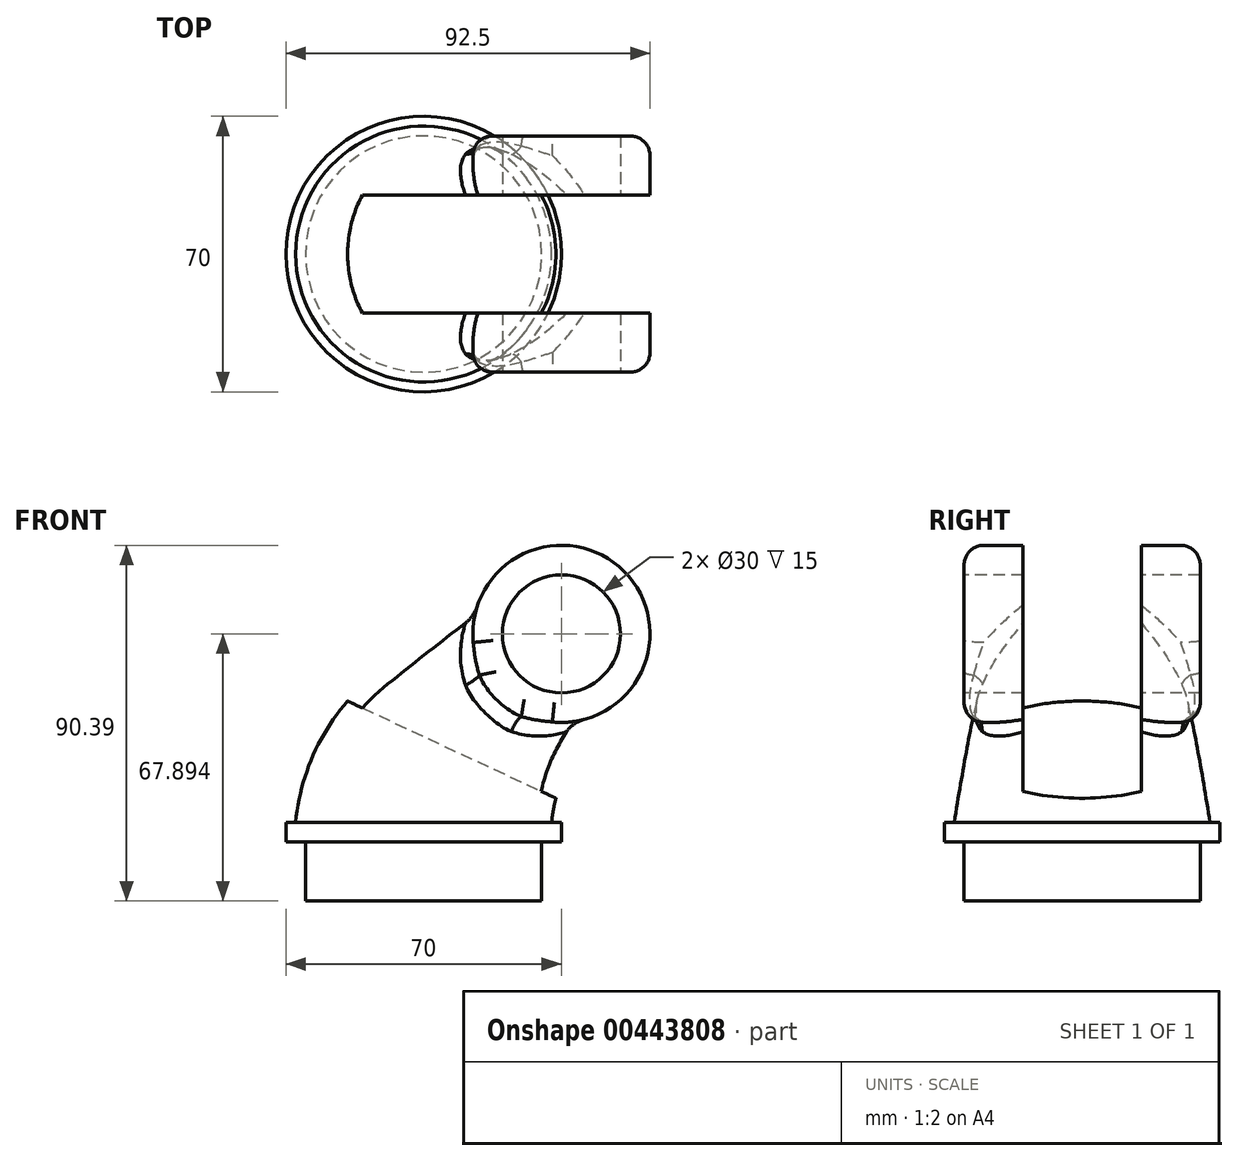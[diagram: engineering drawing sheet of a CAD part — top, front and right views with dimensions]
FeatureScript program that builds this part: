
annotation { "Feature Type Name" : "Feature", "Feature Type Description" : "" }
export const myFeature = defineFeature(function(context is Context, id is Id, definition is map)
    precondition{}
    {
        {
            var Q0;
            Q0=qCreatedBy(makeId("Top.planeOp"),FACE);
            var sketch = newSketch(context, id + "F0", { "sketchPlane" : qUnion([Q0])});
            skCircle(sketch, "E0", {"center": v(0, 0) * mm, "radius": 35 * mm});
            skSolve(sketch);
        }
        {
            var Q0;
            Q0 = qSketchRegion(id + "F0", true);
            extrude(context, id + "F1", {"entities" : qUnion([Q0]), "depth" : 5 * mm});
        }
        {
            var Q0;
            Q0=qCreatedBy(makeId("Front.planeOp"),FACE);
            var sketch = newSketch(context, id + "F2", { "sketchPlane" : qUnion([Q0])});
            skArc(sketch, "E1", {"start": v(17.6, 38.3) * mm, "mid": v(5.55, 23.37) * mm, "end": v(0, 5) * mm});
            skLineSegment(sketch, "E2", {"start": v(17.6, 38.3) * mm, "end": v(35, 52.9) * mm});
            skSolve(sketch);
        }
        {
            var Q0;
            Q0=sQuery(id+"F2.wireOp",EDGE,"E2");
            var Q1;
            Q1=sQuery(id+"F2.wireOp",VERTEX,"E2.end");
            cPlane(context, id + "F3", {"entities" : qUnion([Q0, Q1]), "cplaneType" : CPlaneType.LINE_POINT, "offset" : 25 * mm, "width" : 150 * mm, "height" : 150 * mm});
        }
        {
            var Q0;
            Q0=qCreatedBy(id+"F3.planeOp",FACE);
            var sketch = newSketch(context, id + "F4", { "sketchPlane" : qUnion([Q0])});
            skCircle(sketch, "E3", {"center": v(0, 18.02) * mm, "radius": 22.5 * mm});
            skSolve(sketch);
        }
        {
            var Q0;
            Q0=makeQuery(id+"F1.opExtrude","CAP_FACE",FACE,{"disambiguationData":[OSD([sQuery(id+"F0.wireOp",EDGE,"E0")])],"isStart":false});
            var sketch = newSketch(context, id + "F5", { "sketchPlane" : qUnion([Q0])});
            skCircle(sketch, "E4", {"center": v(0, 0) * mm, "radius": 32.5 * mm});
            skSolve(sketch);
        }
        {
            var Q0;
            Q0=qCreatedBy(makeId("Front.planeOp"),FACE);
            var sketch = newSketch(context, id + "F6", { "sketchPlane" : qUnion([Q0])});
            skArc(sketch, "E5", {"start": v(-13.25, 41.78) * mm, "mid": v(-26.5, 25.3) * mm, "end": v(-32.5, 5) * mm});
            skLineSegment(sketch, "E6", {"start": v(-13.25, 41.78) * mm, "end": v(20.54, 70.13) * mm});
            skSolve(sketch);
        }
        {
            var Q0;
            Q0=qCreatedBy(makeId("Front.planeOp"),FACE);
            var sketch = newSketch(context, id + "F7", { "sketchPlane" : qUnion([Q0])});
            skArc(sketch, "E7", {"start": v(48.46, 34.82) * mm, "mid": v(37.6, 21.45) * mm, "end": v(32.5, 5) * mm});
            skLineSegment(sketch, "E8", {"start": v(48.46, 34.82) * mm, "end": v(49.46, 35.66) * mm});
            skSolve(sketch);
        }
        {
            var Q1;
            Q1=makeQuery(id+"F5.imprint","IMPRINT",FACE,{"disambiguationData":[TD([[makeQuery(id+"F5.imprint","IMPRINT",EDGE,{"derivedFrom":sQuery(id+"F5.wireOp",EDGE,"E4")}),1.0]])]});
            var Q2;
            Q2=makeQuery(id+"F4.imprint","IMPRINT",FACE,{"disambiguationData":[TD([[makeQuery(id+"F4.imprint","IMPRINT",EDGE,{"derivedFrom":sQuery(id+"F4.wireOp",EDGE,"E3")}),1.0]])]});
            var Q3;
            Q3 = qConstructionFilter(qBodyType(qCreatedBy(id + "F6" ,EDGE), BodyType.WIRE), ConstructionObject.NO);
            var Q4;
            Q4 = qConstructionFilter(qBodyType(qCreatedBy(id + "F7" ,EDGE), BodyType.WIRE), ConstructionObject.NO);
            loft(context, id + "F8", {"operationType" : NewBodyOperationType.ADD, "addGuides" : true, "sheetProfilesArray" : [{ "sheetProfileEntities" : qUnion([Q1]) }, { "sheetProfileEntities" : qUnion([Q2]) }], "guidesArray" : [{ "guideEntities" : qUnion([Q3]), "guideDerivativeType" : LoftGuideDerivativeType.DEFAULT, "guideDerivativeMagnitude" : 1 }, { "guideEntities" : qUnion([Q4]), "guideDerivativeType" : LoftGuideDerivativeType.DEFAULT, "guideDerivativeMagnitude" : 1 }]});
        }
        {
            var Q0;
            Q0=qCreatedBy(makeId("Front.planeOp"),FACE);
            var sketch = newSketch(context, id + "F9", { "sketchPlane" : qUnion([Q0])});
            skCircle(sketch, "E9", {"center": v(35, 52.9) * mm, "radius": 22.5 * mm});
            skSolve(sketch);
        }
        {
            var Q0;
            Q0 = qSketchRegion(id + "F9", true);
            extrude(context, id + "F10", {"entities" : qUnion([Q0]), "operationType" : NewBodyOperationType.ADD, "endBound" : BoundingType.SYMMETRIC, "depth" : 60 * mm});
        }
        {
            var Q0;
            Q0=makeQuery(id+"F10.boolean.opBoolean","INTERSECT",EDGE,{"disambiguationData":[OD(1.0)],"derivedFrom":[makeQuery(id+"F8.opLoft","SWEPT_FACE",FACE,{"disambiguationData":[OSD([sQuery(id+"F4.wireOp",EDGE,"E3"),sQuery(id+"F5.wireOp",EDGE,"E4"),sQuery(id+"F6.wireOp",VERTEX,"E6.start"),sQuery(id+"F6.wireOp",EDGE,"E5"),sQuery(id+"F6.wireOp",EDGE,"E6"),sQuery(id+"F7.wireOp",VERTEX,"E8.start"),sQuery(id+"F7.wireOp",EDGE,"E7"),sQuery(id+"F7.wireOp",EDGE,"E8")])]}),makeQuery(id+"F10.opExtrude","SWEPT_FACE",FACE,{"disambiguationData":[OSD([sQuery(id+"F9.wireOp",EDGE,"E9")])]})]});
            var Q1;
            Q1=makeQuery(id+"F10.boolean.opBoolean","INTERSECT",EDGE,{"disambiguationData":[OD(0.0)],"derivedFrom":[makeQuery(id+"F8.opLoft","SWEPT_FACE",FACE,{"disambiguationData":[OSD([sQuery(id+"F4.wireOp",EDGE,"E3"),sQuery(id+"F5.wireOp",EDGE,"E4"),sQuery(id+"F6.wireOp",VERTEX,"E6.start"),sQuery(id+"F6.wireOp",EDGE,"E5"),sQuery(id+"F6.wireOp",EDGE,"E6"),sQuery(id+"F7.wireOp",VERTEX,"E8.start"),sQuery(id+"F7.wireOp",EDGE,"E7"),sQuery(id+"F7.wireOp",EDGE,"E8")])]}),makeQuery(id+"F10.opExtrude","SWEPT_FACE",FACE,{"disambiguationData":[OSD([sQuery(id+"F9.wireOp",EDGE,"E9")])]})]});
            fillet(context, id + "F11", {"entities" : qUnion([Q0, Q1]), "radius" : 5 * mm, "tangentPropagation" : true, "allowEdgeOverflow" : false});
        }
        {
            var Q0;
            Q0=makeQuery(id+"F10.opExtrude","CAP_FACE",FACE,{"disambiguationData":[OSD([sQuery(id+"F9.wireOp",EDGE,"E9")])],"isStart":true});
            var Q1;
            Q1=makeQuery(id+"F10.opExtrude","CAP_FACE",FACE,{"disambiguationData":[OSD([sQuery(id+"F9.wireOp",EDGE,"E9")])],"isStart":false});
            fillet(context, id + "F12", {"entities" : qUnion([Q0, Q1]), "radius" : 5 * mm, "tangentPropagation" : true, "allowEdgeOverflow" : false});
        }
        {
            var Q0;
            Q0=makeQuery(id+"F10.opExtrude","CAP_FACE",FACE,{"disambiguationData":[OSD([sQuery(id+"F9.wireOp",EDGE,"E9")])],"isStart":false});
            var sketch = newSketch(context, id + "F13", { "sketchPlane" : qUnion([Q0])});
            skCircle(sketch, "E10", {"center": v(35, 52.9) * mm, "radius": 15 * mm});
            skSolve(sketch);
        }
        {
            var Q0;
            Q0 = qSketchRegion(id + "F13", true);
            extrude(context, id + "F14", {"entities" : qUnion([Q0]), "operationType" : NewBodyOperationType.REMOVE, "endBound" : BoundingType.THROUGH_ALL, "oppositeDirection" : true, "depth" : 25 * mm});
        }
        {
            var Q0;
            Q0=qCreatedBy(makeId("Front.planeOp"),FACE);
            var sketch = newSketch(context, id + "F15", { "sketchPlane" : qUnion([Q0])});
            skLineSegment(sketch, "E11", {"start": v(-104.18, 75.4) * mm, "end": v(57.5, 0) * mm});
            skLineSegment(sketch, "E12", {"start": v(57.5, 75.4) * mm, "end": v(57.5, 0) * mm});
            skLineSegment(sketch, "E13", {"start": v(-104.18, 75.4) * mm, "end": v(57.5, 75.4) * mm});
            skSolve(sketch);
        }
        {
            var Q0;
            Q0 = qSketchRegion(id + "F15", true);
            extrude(context, id + "F16", {"entities" : qUnion([Q0]), "operationType" : NewBodyOperationType.REMOVE, "endBound" : BoundingType.SYMMETRIC, "oppositeDirection" : true, "depth" : 30 * mm});
        }
        {
            var Q0;
            Q0=qCreatedBy(makeId("Front.planeOp"),FACE);
            var sketch = newSketch(context, id + "F17", { "sketchPlane" : qUnion([Q0])});
            skLineSegment(sketch, "E14.bottom", {"start": v(0, 0) * mm, "end": v(-30, 0) * mm});
            skLineSegment(sketch, "E14.top", {"start": v(0, -15) * mm, "end": v(-30, -15) * mm});
            skLineSegment(sketch, "E14.left", {"start": v(0, 0) * mm, "end": v(0, -15) * mm});
            skLineSegment(sketch, "E14.right", {"start": v(-30, 0) * mm, "end": v(-30, -15) * mm});
            skSolve(sketch);
        }
        {
            var Q0;
            Q0 = qSketchRegion(id + "F17", true);
            var Q1;
            Q1=sQuery(id+"F17.wireOp",EDGE,"E14.left");
            revolve(context, id + "F18", {"operationType" : NewBodyOperationType.ADD, "entities" : qUnion([Q0]), "axis" : qUnion([Q1]), "revolveType" : RevolveType.FULL});
        }
    });
